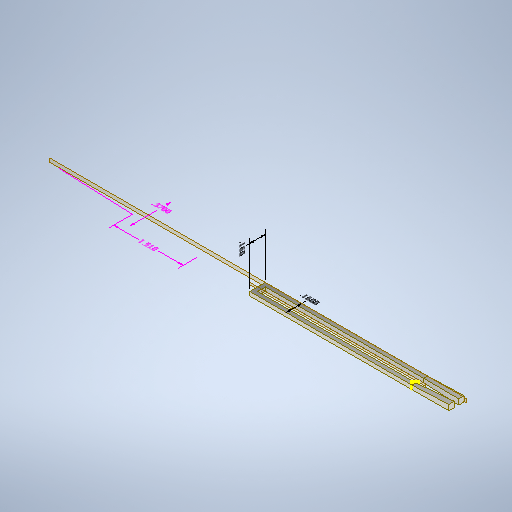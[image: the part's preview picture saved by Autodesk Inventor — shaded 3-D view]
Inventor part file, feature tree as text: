
AUTODESK INVENTOR PART (.ipt)
format: ipt  version: 2025.2 (Build 292293000, 293)  size: 308,224 bytes
history: native  units: in
note: dims shown in document units (in); Inventor stores cm internally (conversion verified against a paired STEP export)
features: other x6, plane x4, sketch x4, sweep x1, loft x1, mirror x1, projected_geometry x1
ambient origin geometry x8: Origin, YZ Plane, XZ Plane, XY Plane, X Axis, Y Axis, Z Axis, Center Point
bodies: Solid1 (feature_tree)
feature tree (18):
  other  "Annotations"
  sweep  "Sweep1"
  plane  "Work Plane1"
  plane  "Work Plane2"
  plane  "Work Plane4"
  sketch  "Sketch15"  dims[d86=-0.1175in]
  sketch  "Sketch16"  dims[d89=0.1in d90=0.0in d91=0.0in d92=0.0in d98=0.04in d99=0.04in d100=0.055in d102=0.055in d104=0.0in d109=0.0in d110=90.0deg d111=0.0in d112=90.0deg d116=-0.08in d113=0.0in d114=0.3937in d115=0.16in d117=0.086in d118=0.3123in d119=0.16in d42=0.2341in d43=0.169in d44=0.37in d48=0.2141in d49=0.2512in d50=1.51in]
  loft  "Loft3"
  plane  "Work Plane5"
  mirror  "Mirror3"
  sketch  "Sketch1"  dims[d6=0.0in d7=0.0in d11=0.375in d19=-0.25in]
  sketch  "Sketch2"  dims[d69=1.625in d70=1.625in]
  projected_geometry  "Projected Loop1"
  other  "Edges4"
  other  "Linear Dimension 1"
  other  "Linear Dimension 3"
  other  "Linear Dimension 4"
  other  "Linear Dimension 5"
